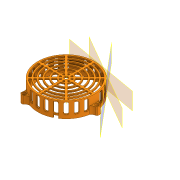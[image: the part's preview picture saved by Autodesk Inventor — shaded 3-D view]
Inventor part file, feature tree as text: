
AUTODESK INVENTOR PART (.ipt)
format: ipt  version: 2020.3 (Build 243373000, 373)  size: 1,065,472 bytes
history: native  units: mm
features: other x23, extrude x11, sketch x8, plane x3, pattern_circular x2, fillet x1
ambient origin geometry x8: Origin, YZ Plane, XZ Plane, XY Plane, X Axis, Y Axis, Z Axis, Center Point
bodies: Body1 (feature_tree)
feature tree (48):
  sketch  "Sketch1"  dims[d0=95.0mm d1=120.0deg]
  extrude  "Extrusion9"  TaperAngle=120.0deg  [1 undecoded]
  extrude  "Extrusion13"  Depth=16.0mm
  extrude  "Extrusion14"  Depth=6.5mm
  extrude  "Extrusion16"  Depth=10.0mm
  extrude  "Extrusion17"  Depth=1.2mm
  plane  "Work Plane5"
  plane  "Work Plane6"
  plane  "Work Plane7"
  sketch  "Sketch12"  dims[d4=3.4mm d5=6.5mm]
  sketch  "Sketch13"  dims[d7=10.0mm d8=3.6mm]
  sketch  "Sketch14"  dims[d9=2.4mm d10=1.2mm]
  extrude  "Extrusion21"  Depth=9.8mm
  extrude  "Extrusion22"  Depth=2.0mm
  extrude  "Extrusion23"  Depth=2.0mm
  extrude  "Extrusion24"  TaperAngle=60.0deg  [1 undecoded]
  extrude  "Extrusion25"  Depth=10.0mm
  pattern_circular  "Circular Pattern3"  [2 undecoded]
  fillet  "Fillet3"  Radius=6.1mm
  pattern_circular  "Circular Pattern4"  Angle=60.0deg  [1 undecoded]
  extrude  "Extrusion26"  Depth=10.0mm
  sketch  "Sketch8"  dims[d2=120.0deg d3=16.0mm]
  sketch  "Sketch15"  dims[d13=30.0mm d15=360.0deg d17=9.8mm]
  sketch  "Sketch16"  dims[d18=12.0mm d19=2.0mm]
  other  "Work Axis1"
  other  "Work Axis2"
  other  "Work Axis3"
  other  "Work Axis4"
  other  "Work Axis5"
  other  "Work Axis6"
  other  "Work Axis7"
  other  "Work Axis8"
  other  "Work Axis9"
  other  "Work Axis10"
  other  "Work Axis11"
  other  "Work Axis12"
  other  "Work Axis13"
  other  "Work Axis14"
  other  "Work Axis15"
  other  "Work Axis16"
  other  "Work Axis17"
  other  "Work Axis18"
  other  "Work Axis19"
  other  "Work Axis20"
  other  "Work Axis21"
  other  "Work Axis22"
  other  "Work Axis23"
  sketch  "Sketch17"  dims[d20=6.0mm d21=2.0mm d23=60.0deg d24=6.1mm d25=8.0mm d26=6.1mm d27=60.0deg d28=3.490659mm d29=3.490659mm d56=40.0mm d57=60.0mm d58=3.2mm d59=1.3mm d60=1.0mm d61=1.0mm d62=1.3mm d64=3.0mm d65=8.0mm d66=6.0mm d74=90.0mm d75=26.0mm d76=0.0mm d83=4.2mm d84=0.0mm d85=8.4mm d86=0.0mm d99=12.5mm d100=0.0mm d101=6.5mm d102=6.0mm d103=6.0mm d104=3.0mm d105=0.0mm d115=4.0mm d116=4.0mm d122=90.0deg d123=90.0deg d124=90.0deg d126=5.5mm d127=5.5mm d128=5.5mm d129=10.0mm d130=0.0mm d131=10.0mm d132=0.0mm d133=10.0mm d134=0.0mm d135=2.0mm d136=0.0mm d137=18.0mm d138=2.0mm d139=10.0mm d140=0.0mm d141=240.0mm d142=360.0deg d155=45.0deg d157=5.0mm d158=95.0mm d159=90.0mm d160=6.0mm d161=7.0mm d162=8.0mm d163=9.0mm d164=8.0mm d169=1.5mm d170=1.5mm d172=1.5mm d173=1.5mm d174=1.0mm d175=40.0mm d176=360.0deg d178=6.0mm d179=10.0mm d180=0.0mm d72=0.5mm d73=0.872665mm d106=0.5mm d107=0.872665mm d108=0.5mm d109=0.872665mm d120=0.5mm d121=0.872665mm d125=0.872665mm]
note: 5 required parameter values undecoded (feature->parameter linkage not recoverable at this tier; creation-order binding heuristic only, values carry confidence <= 0.55)
